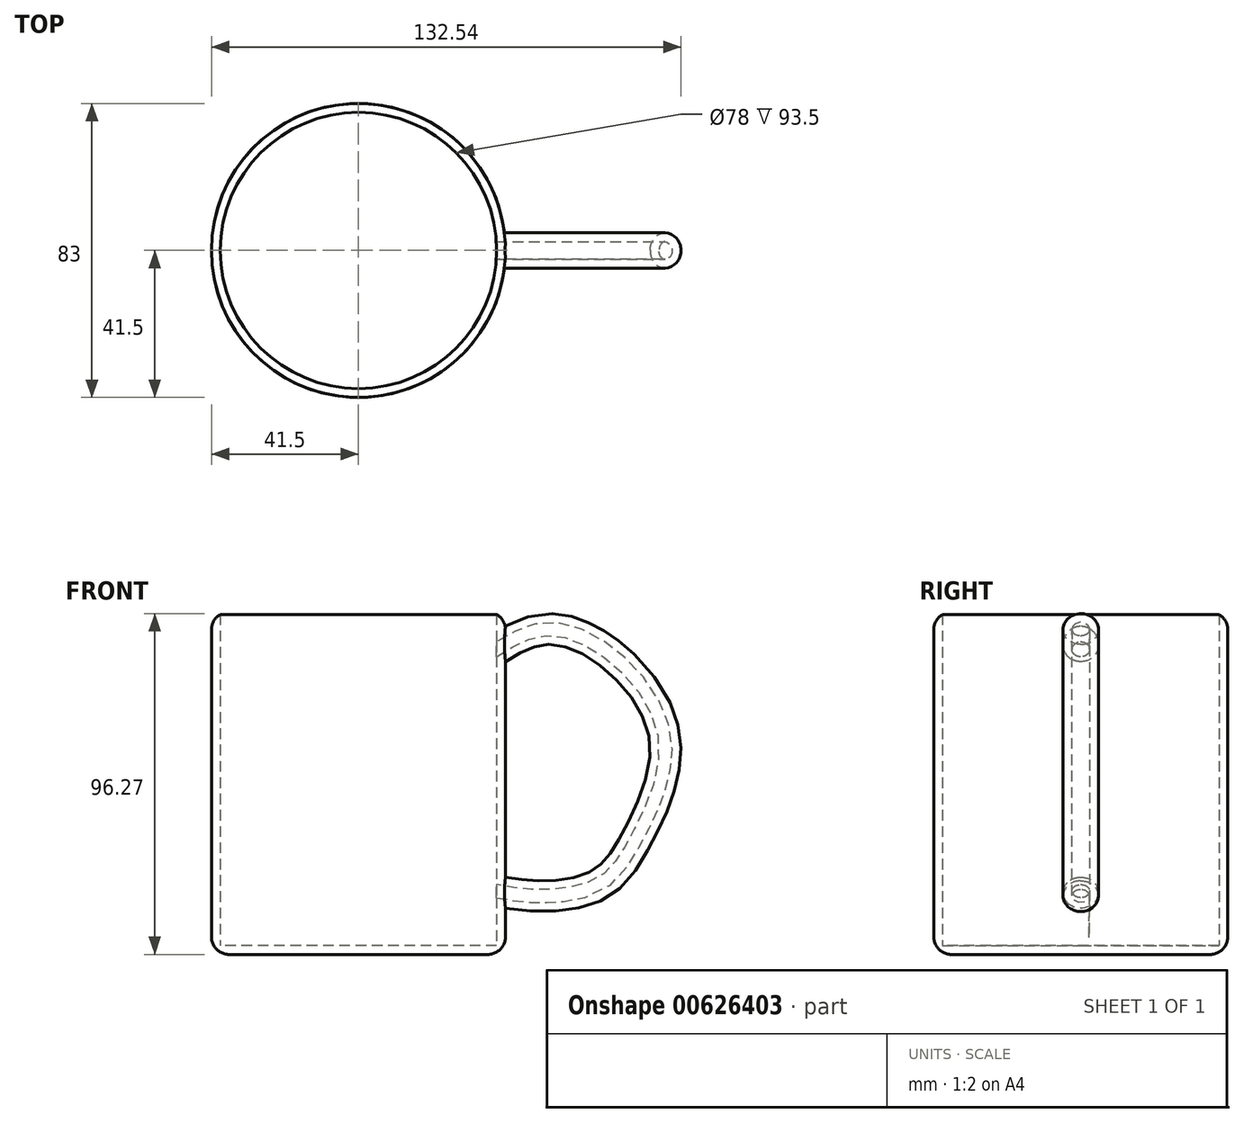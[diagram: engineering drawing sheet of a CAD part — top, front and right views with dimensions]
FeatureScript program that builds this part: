
annotation { "Feature Type Name" : "Feature", "Feature Type Description" : "" }
export const myFeature = defineFeature(function(context is Context, id is Id, definition is map)
    precondition{}
    {
        {
            var Q0;
            Q0=qCreatedBy(makeId("Top.planeOp"),FACE);
            var sketch = newSketch(context, id + "F0", { "sketchPlane" : qUnion([Q0])});
            skCircle(sketch, "E0", {"center": v(0, 0) * mm, "radius": 41.5 * mm});
            skSolve(sketch);
        }
        {
            var Q0;
            Q0 = qSketchRegion(id + "F0", true);
            extrude(context, id + "F1", {"entities" : qUnion([Q0]), "depth" : 96 * mm, "offsetDistance" : 25 * mm});
        }
        {
            var Q0;
            Q0=qCreatedBy(makeId("Front.planeOp"),FACE);
            var sketch = newSketch(context, id + "F2", { "sketchPlane" : qUnion([Q0])});
            skFitSpline(sketch, "E1", {"points": [v(37.79, 83.98) * mm, v(52.74, 90.5) * mm, v(70.95, 83.37) * mm, v(85.26, 60) * mm, v(77.45, 33.35) * mm, v(67.37, 21) * mm, v(50.8, 17.73) * mm, v(36.16, 19.66) * mm], "startDerivative": vector(110.6, 70.28) * mm, "endDerivative": vector(-112.68, 21.97) * mm});
            skSolve(sketch);
        }
        {
            var Q0;
            Q0=qCreatedBy(makeId("Right.planeOp"),FACE);
            cPlane(context, id + "F3", {"entities" : qUnion([Q0]), "cplaneType" : CPlaneType.OFFSET, "offset" : 41.5 * mm, "width" : 150 * mm, "height" : 150 * mm});
        }
        {
            var Q0;
            Q0=qCreatedBy(id+"F3.planeOp",FACE);
            var sketch = newSketch(context, id + "F4", { "sketchPlane" : qUnion([Q0])});
            skCircle(sketch, "E2", {"center": v(0, 87.68) * mm, "radius": 5 * mm});
            skSolve(sketch);
        }
        {
            var Q0;
            Q0=makeQuery(id+"F4.imprint","IMPRINT",FACE,{"disambiguationData":[TD([[makeQuery(id+"F4.imprint","IMPRINT",EDGE,{"derivedFrom":sQuery(id+"F4.wireOp",EDGE,"E2")}),1.0]])]});
            var Q1;
            Q1=sQuery(id+"F2.wireOp",EDGE,"E1");
            sweep(context, id + "F5", {"operationType" : NewBodyOperationType.ADD, "profiles" : qUnion([Q0]), "path" : qUnion([Q1])});
        }
        {
            var Q0;
            Q0=makeQuery(id+"F1.opExtrude","CAP_FACE",FACE,{"disambiguationData":[OSD([sQuery(id+"F0.wireOp",EDGE,"E0")])],"isStart":false});
            shell(context, id + "F6", {"entities" : qUnion([Q0]), "thickness" : 2.5 * mm});
        }
        {
            var Q0;
            Q0=makeQuery(id+"F1.opExtrude","CAP_EDGE",EDGE,{"disambiguationData":[OSD([sQuery(id+"F0.wireOp",EDGE,"E0")])],"isStart":false});
            var Q1;
            Q1=makeQuery(id+"F1.opExtrude","CAP_EDGE",EDGE,{"disambiguationData":[OSD([sQuery(id+"F0.wireOp",EDGE,"E0")])],"isStart":true});
            fillet(context, id + "F7", {"entities" : qUnion([Q0, Q1]), "radius" : 5 * mm, "tangentPropagation" : true, "allowEdgeOverflow" : false});
        }
    });
